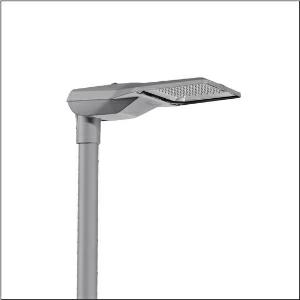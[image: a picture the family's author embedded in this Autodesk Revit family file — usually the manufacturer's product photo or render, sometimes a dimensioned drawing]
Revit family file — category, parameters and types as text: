
# Revit family: streetlight_sl_21_iq_midi___st1_0ab_5xe3m31v08mb_24a1
name_source: partatom
category: Lighting Fixtures
units: mm (PartAtom-declared; Revit-internal decimal feet)

## family parameters
Cut with Voids When Loaded = No
Host = Face
Light Source = No
Part Type = Normal
Room Calculation Point = No
Round Connector Dimension = Use Diameter
Shared = No

## types (1)
- --- (1 x LED, 16140 lm, 129.3 W, 3000K)
    Apparent Load = 129 VA
    CIE Flux Codes = 38 73 97 100 100
    Color Rendering = 70
    Color Temperature = 3000K
    Default Elevation = 1800 mm
    Description = Streetlight SL 21 iQ midi, mast luminaire, primary light control with lens, of PMMA, primary optical cover: cover, of toughened safety glass, transparent, light distribution: ST1.0aB, light emission: direct distribution, primary light characteristic: asymmetric, installation type: post-top, side-entry, LED, High Power LED, rated luminous flux: 16.140lm, luminous efficacy: 125lm/W, light colour: 730, colour temperature: 3000K, control: pre-setting: logarithmic dimming characteristic, Street-Remote, Auto-Match, Temp-Guard, Lumen-Switch, Night-Set, Smart-Wire, Light-Fading, Desk-Remote (wireless, voltage-free reading and setting of iQ features in the workshop via application-optimized NFC function/RFID function), optimised constant luminous flux control (CLO 2.0), mains connection: 230..240V, AC, 50/60Hz, start of lifetime: 129W, end of service life: 142W, reduction: 56W, luminaire housing, of diecast aluminium, powder-coated, Siteco® metallic grey (DB 702S), corrosivity category C5 mid according to DIN EN ISO 12944, please order mast flange separately, inclination adjustable: 0°, 5°, 10°, 15°, sealing non-destructively replaceable, multi-level sealing system, length: 644mm, width: 335mm, height: 110mm, mast flange for spigot size: 42mm (side-entry): 5XC10008XM4, 60/48mm (side-entry/post-top): 5XC10108XM2, 76/60mm (side-entry/post-top): 5XC10108XM1, Smart Interface above, protection rating (complete): IP66, insulation class (complete): insulation class II (safety insulation), certification: CE, ENEC, ENEC+, VDE, impact resistance: IK09, permissible operating ambient temperature for outdoor applications: -40..+50°C, standard-compliant lighting for roads and squares, packaging unit: 1 piece

Light Distribution: ST1.0aB
    Height = 111 mm
    Lamp = 1 x LED
    Lamp Light Flux = 16140 lm
    Lamp Power = 129.3 W
    Lamp count = 1
    Length = 644 mm
    Luminous efficacy = 125 lm/W
    Manufacturer = Siteco
    ModVariant = No
    Model = 5XE3M31V08MB
    Number of Poles = 1
    OnlyDefault = Yes
    Power Factor = 1
    Product Name = Streetlight SL 21 iQ midi | ST1.0aB
    Product group = mast luminaire | pylon top
    ProductGroupID = 6100
    Protection Class = Protection class II
    Protection Degree = IP 66
    RLX_Detail_Level = 1
    RLX_Emergency_Light_Flux = 0 lm
    RLX_Emergency_Type = 0
    RLX_Emergency_Type_DB = No
    RlxData = <blob elided: 90889 chars, md5=93f3b9eb>
    Socket = socket
    Standby Power = 0 W
    System Light Flux = 16141 lm
    System Power = 129 W
    Type Comments = factory setting: luminous flux: 100 % | dim-lin: 254 | 672 mA
    Type Image = l_1004302.jpg
    URL = http://relux.com
    VarID = @adj_081171
    Voltage = 0 V
    Weight = 0.00 kg
    Width = 336 mm

## geometry (parser evidence)
native form markers: Blend x4, Sweep x11
no freeform markers — native parametric forms only
